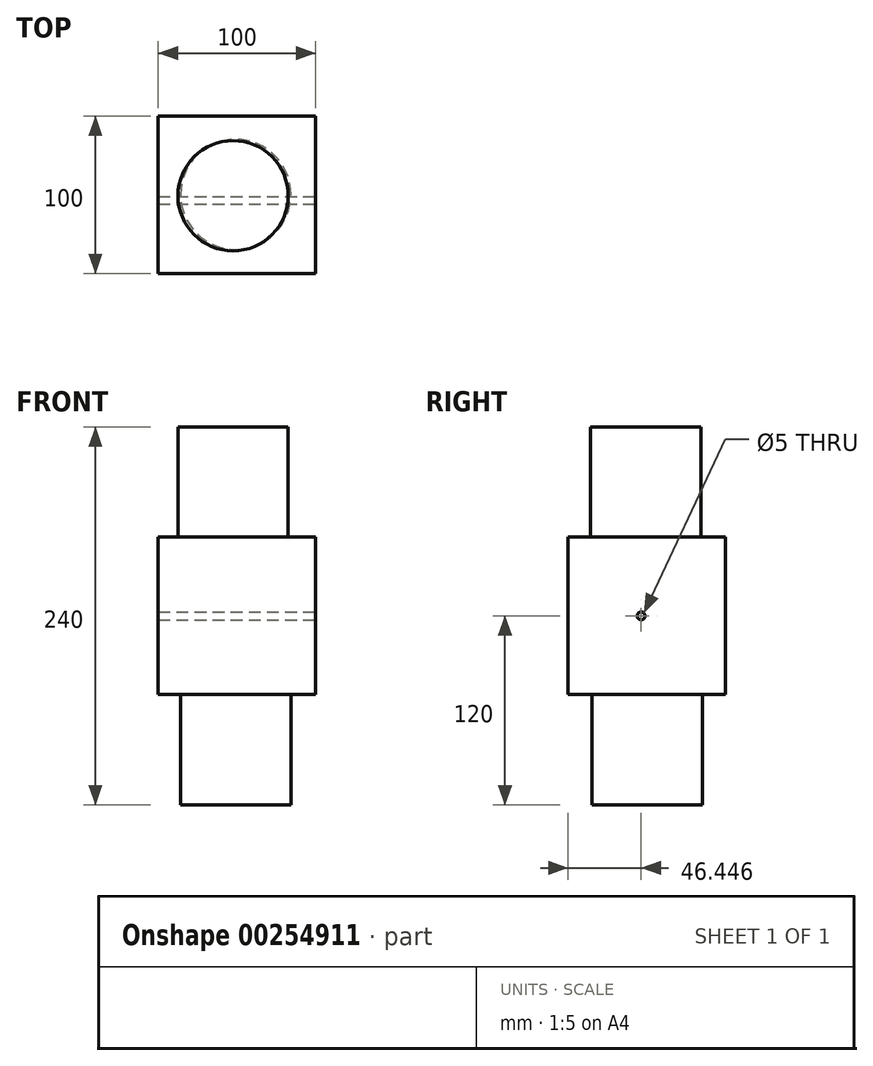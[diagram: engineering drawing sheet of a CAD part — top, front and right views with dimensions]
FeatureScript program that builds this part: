
annotation { "Feature Type Name" : "Feature", "Feature Type Description" : "" }
export const myFeature = defineFeature(function(context is Context, id is Id, definition is map)
    precondition{}
    {
        {
            var Q0;
            Q0=qCreatedBy(makeId("Front.planeOp"),FACE);
            var sketch = newSketch(context, id + "F0", { "sketchPlane" : qUnion([Q0])});
            skLineSegment(sketch, "E0.bottom", {"start": v(0, 0) * mm, "end": v(100, 0) * mm});
            skLineSegment(sketch, "E0.top", {"start": v(0, 100) * mm, "end": v(100, 100) * mm});
            skLineSegment(sketch, "E0.left", {"start": v(0, 0) * mm, "end": v(0, 100) * mm});
            skLineSegment(sketch, "E0.right", {"start": v(100, 0) * mm, "end": v(100, 100) * mm});
            skSolve(sketch);
        }
        {
            var Q0;
            Q0 = qSketchRegion(id + "F0", true);
            extrude(context, id + "F1", {"entities" : qUnion([Q0]), "depth" : 100 * mm});
        }
        {
            var Q0;
            Q0=makeQuery(id+"F1.opExtrude","SWEPT_FACE",FACE,{"disambiguationData":[OSD([sQuery(id+"F0.wireOp",EDGE,"E0.top")])]});
            var sketch = newSketch(context, id + "F2", { "sketchPlane" : qUnion([Q0])});
            skCircle(sketch, "E1", {"center": v(47.52, -50.62) * mm, "radius": 35 * mm});
            skSolve(sketch);
        }
        {
            var Q0;
            Q0 = qSketchRegion(id + "F2", true);
            extrude(context, id + "F3", {"entities" : qUnion([Q0]), "operationType" : NewBodyOperationType.ADD, "depth" : 70 * mm});
        }
        {
            var Q0;
            Q0=makeQuery(id+"F1.opExtrude","SWEPT_FACE",FACE,{"disambiguationData":[OSD([sQuery(id+"F0.wireOp",EDGE,"E0.bottom")])]});
            var sketch = newSketch(context, id + "F4", { "sketchPlane" : qUnion([Q0])});
            skCircle(sketch, "E2", {"center": v(49.18, 49.72) * mm, "radius": 35 * mm});
            skSolve(sketch);
        }
        {
            var Q0;
            Q0 = qSketchRegion(id + "F4", true);
            extrude(context, id + "F5", {"entities" : qUnion([Q0]), "operationType" : NewBodyOperationType.ADD, "depth" : 70 * mm});
        }
        {
            var Q0;
            Q0=makeQuery(id+"F1.opExtrude","SWEPT_FACE",FACE,{"disambiguationData":[OSD([sQuery(id+"F0.wireOp",EDGE,"E0.right")])]});
            var sketch = newSketch(context, id + "F6", { "sketchPlane" : qUnion([Q0])});
            skCircle(sketch, "E3", {"center": v(-53.55, 50) * mm, "radius": 35 * mm});
            skPoint(sketch, "E3.centerSnap0", {"position": v(0, 50) * mm});
            skSolve(sketch);
        }
        {
            var Q0;
            Q0=sQuery(id+"F6.wireOp",VERTEX,"E3.center");
            var Q1;
            Q1=makeQuery(id+"F1.opExtrude","SWEPT_BODY",BODY,{"disambiguationData":[OSD([sQuery(id+"F0.wireOp",EDGE,"E0.bottom"),sQuery(id+"F0.wireOp",EDGE,"E0.top"),sQuery(id+"F0.wireOp",EDGE,"E0.left"),sQuery(id+"F0.wireOp",EDGE,"E0.right")])]});
            hole(context, id + "F7", {"style" : HoleStyle.SIMPLE, "endStyle" : HoleEndStyle.THROUGH, "holeDiameter" : 5 * mm, "tappedDepth" : 12 * mm, "tapClearance" : 3, "locations" : qUnion([Q0]), "scope" : qUnion([Q1])});
        }
    });
